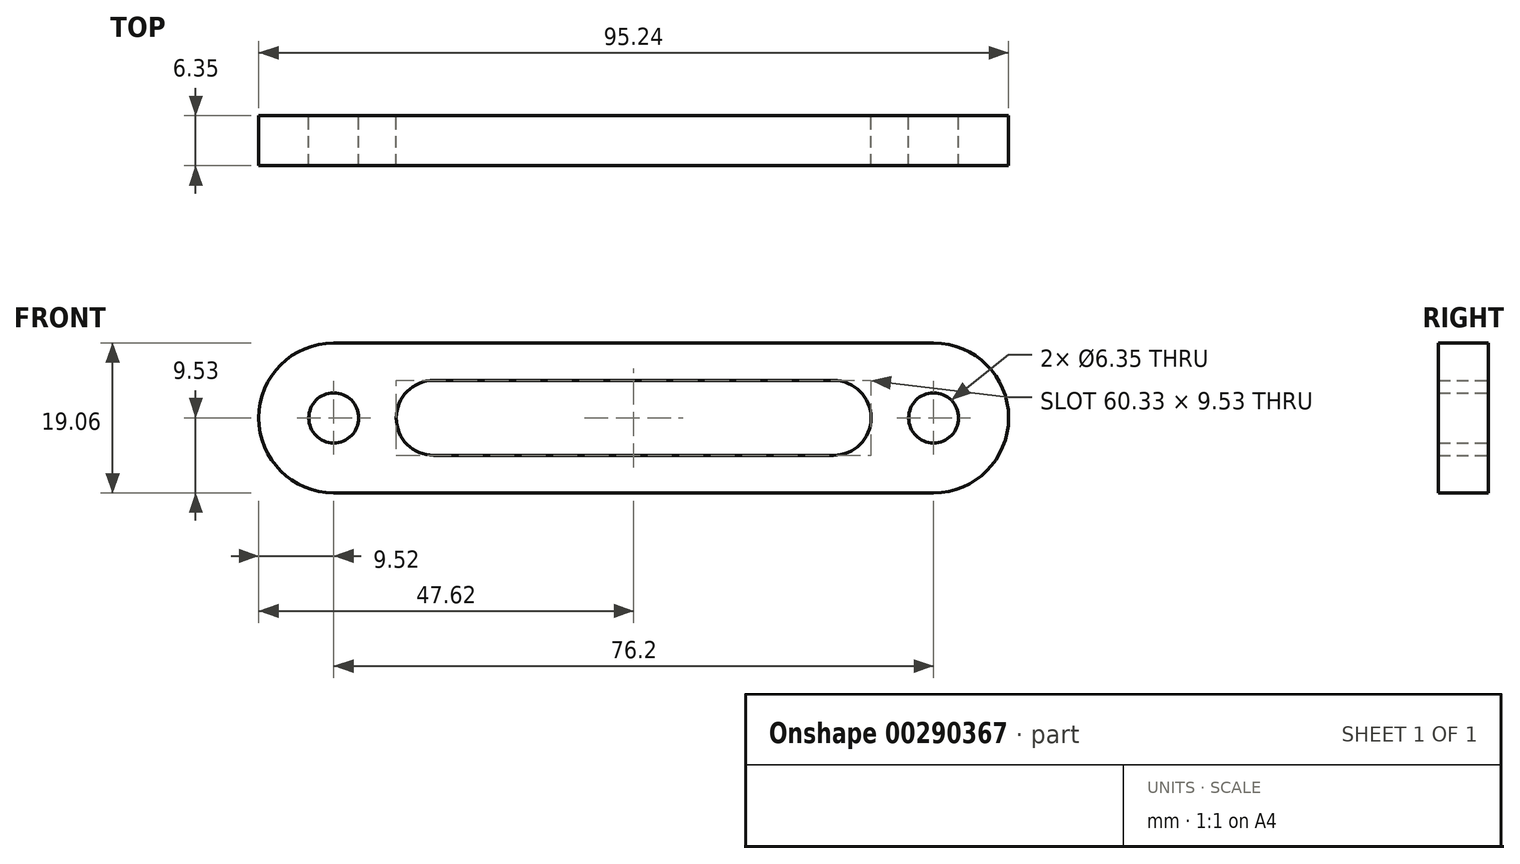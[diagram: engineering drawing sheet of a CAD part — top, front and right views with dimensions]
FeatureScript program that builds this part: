
annotation { "Feature Type Name" : "Feature", "Feature Type Description" : "" }
export const myFeature = defineFeature(function(context is Context, id is Id, definition is map)
    precondition{}
    {
        {
            var Q0;
            Q0=qCreatedBy(makeId("Front.planeOp"),FACE);
            var sketch = newSketch(context, id + "F0", { "sketchPlane" : qUnion([Q0])});
            skLineSegment(sketch, "E0.bottom", {"start": v(-38.1, 9.53) * mm, "end": v(38.1, 9.53) * mm});
            skLineSegment(sketch, "E0.top", {"start": v(-38.1, -9.53) * mm, "end": v(38.1, -9.53) * mm});
            skLineSegment(sketch, "E0.left", {"start": v(-38.1, 9.53) * mm, "end": v(-38.1, -9.53) * mm});
            skLineSegment(sketch, "E0.right", {"start": v(38.1, 9.53) * mm, "end": v(38.1, -9.53) * mm});
            skPoint(sketch, "E1", {"position": v(0, 9.53) * mm});
            skPoint(sketch, "E2", {"position": v(38.1, 0) * mm});
            skArc(sketch, "E3", {"start": v(-38.1, 9.53) * mm, "mid": v(-47.63, 0) * mm, "end": v(-38.1, -9.53) * mm});
            skArc(sketch, "E4", {"start": v(38.1, -9.53) * mm, "mid": v(47.62, 0) * mm, "end": v(38.1, 9.53) * mm});
            skCircle(sketch, "E5", {"center": v(-38.1, 0) * mm, "radius": 3.18 * mm});
            skCircle(sketch, "E6", {"center": v(38.1, 0) * mm, "radius": 3.18 * mm});
            skLineSegment(sketch, "E7.bottom", {"start": v(-25.4, 4.76) * mm, "end": v(25.4, 4.76) * mm});
            skLineSegment(sketch, "E7.top", {"start": v(-25.4, -4.76) * mm, "end": v(25.4, -4.76) * mm});
            skLineSegment(sketch, "E7.left", {"start": v(-25.4, 4.76) * mm, "end": v(-25.4, -4.76) * mm});
            skLineSegment(sketch, "E7.right", {"start": v(25.4, 4.76) * mm, "end": v(25.4, -4.76) * mm});
            skPoint(sketch, "E8", {"position": v(0, 4.76) * mm});
            skPoint(sketch, "E9", {"position": v(25.4, 0) * mm});
            skPoint(sketch, "E10", {"position": v(-25.4, 0) * mm});
            skArc(sketch, "E11", {"start": v(-25.4, 4.76) * mm, "mid": v(-30.16, 0) * mm, "end": v(-25.4, -4.76) * mm});
            skArc(sketch, "E12", {"start": v(25.4, -4.76) * mm, "mid": v(30.16, 0) * mm, "end": v(25.4, 4.76) * mm});
            skSolve(sketch);
        }
        {
            var Q0;
            Q0=qSketchRegion(id+"F0",true);
            extrude(context, id + "F1", {"entities" : qUnion([Q0]), "depth" : 6.35 * mm});
        }
    });
